# Revit family: ALT2x2-C135
name_source: partatom
category: Lighting Fixtures
units: mm (PartAtom-declared; Revit-internal decimal feet)

## family parameters
Always vertical = Yes
Cut with Voids When Loaded = No
Host = Ceiling
Light Source = Yes
Maintain Annotation Orientation = No
OmniClass Number = 23.80.70.11.14.17
OmniClass Title = Direct/Indirect
Part Type = Normal
Room Calculation Point = No
Round Connector Dimension = Use Diameter
Shared = No

## types (4) — shared parameters
Assembly Code = D5020200
Color Filter = 16777215
Default Elevation = 0' - 0"
Description = Architectural Recessed Troffer with Regressed Circular Lens
Dimming Lamp Color Temperature Shift = <None>
Emit Shape Visible in Rendering = No
Emit from Rectangle Height = 0' - 0 1/8"
Emit from Rectangle Length = 1' - 11 3/4"
Emit from Rectangle Width = 1' - 11 3/4"
Housing Finish = Metal - Viscor - White
Lamp = LED
Length = 1' - 11 3/4"
Lens Depth = 0' - 0 1/8"
Lens Finish = Acrylic - Viscor - Frosted White
Manufacturer = VISIONEERING by VISCOR
Model = ALT2x2-C135
Tilt Angle = 90.00°
URL = https://viscor.com
Voltage = 120 V
Width = 1' - 11 3/4"

## per-type parameters (varying)
| type | Apparent Load | Lamp Wattage | Photometric Web File |
| ALT2x2-LED840K024LUNV-C135 | 22 VA | 22 VA | ALT2x2-LED840K024LUNV-C135.ies |
| ALT2x2-LED840K034LUNV-C135 | 32 VA | 32 VA | ALT2x2-LED840K034LUNV-C135.ies |
| ALT2x2-LED840K040LUNV-C135 | 38 VA | 38 VA | ALT2x2-LED840K040LUNV-C135.ies |
| ALT2x2-LED840K050LUNV-C135 | 48 VA | 48 VA | ALT2x2-LED840K050LUNV-C135.ies |

## geometry (parser evidence)
native form markers: Sweep x2
no freeform markers — native parametric forms only
